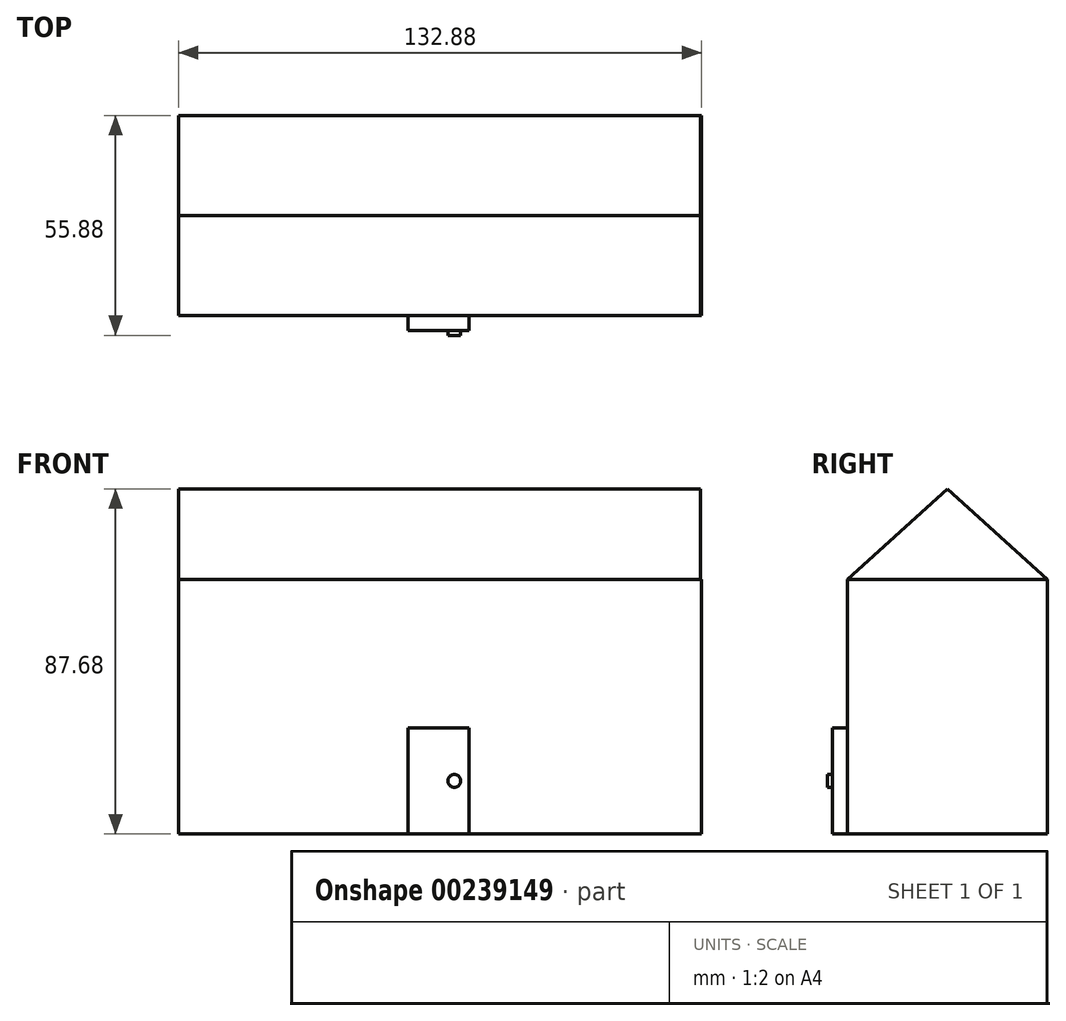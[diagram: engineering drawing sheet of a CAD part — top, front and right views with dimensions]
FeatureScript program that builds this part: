
annotation { "Feature Type Name" : "Feature", "Feature Type Description" : "" }
export const myFeature = defineFeature(function(context is Context, id is Id, definition is map)
    precondition{}
    {
        {
            var Q0;
            Q0=qCreatedBy(makeId("Front.planeOp"),FACE);
            var sketch = newSketch(context, id + "F0", { "sketchPlane" : qUnion([Q0])});
            skLineSegment(sketch, "E0.bottom", {"start": v(-66.44, 32.31) * mm, "end": v(66.44, 32.31) * mm});
            skLineSegment(sketch, "E0.top", {"start": v(-66.44, -32.31) * mm, "end": v(66.44, -32.31) * mm});
            skLineSegment(sketch, "E0.left", {"start": v(-66.44, 32.31) * mm, "end": v(-66.44, -32.31) * mm});
            skLineSegment(sketch, "E0.right", {"start": v(66.44, 32.31) * mm, "end": v(66.44, -32.31) * mm});
            skPoint(sketch, "E0.middle", {"position": v(0, 0) * mm});
            skSolve(sketch);
        }
        {
            var Q0;
            Q0 = qSketchRegion(id + "F0", true);
            extrude(context, id + "F1", {"entities" : qUnion([Q0]), "endBound" : BoundingType.SYMMETRIC, "depth" : 50.8 * mm});
        }
        {
            var Q0;
            Q0=makeQuery(id+"F1.opExtrude","CAP_FACE",FACE,{"disambiguationData":[OSD([sQuery(id+"F0.wireOp",EDGE,"E0.bottom"),sQuery(id+"F0.wireOp",EDGE,"E0.top"),sQuery(id+"F0.wireOp",EDGE,"E0.left"),sQuery(id+"F0.wireOp",EDGE,"E0.right")])],"isStart":false});
            var sketch = newSketch(context, id + "F2", { "sketchPlane" : qUnion([Q0])});
            skLineSegment(sketch, "E1.bottom", {"start": v(7.28, -32.31) * mm, "end": v(-8.2, -32.31) * mm});
            skLineSegment(sketch, "E1.top", {"start": v(7.28, -5.3) * mm, "end": v(-8.2, -5.3) * mm});
            skLineSegment(sketch, "E1.left", {"start": v(7.28, -32.31) * mm, "end": v(7.28, -5.3) * mm});
            skLineSegment(sketch, "E1.right", {"start": v(-8.2, -32.31) * mm, "end": v(-8.2, -5.3) * mm});
            skSolve(sketch);
        }
        {
            var Q0;
            Q0 = qSketchRegion(id + "F2", true);
            extrude(context, id + "F3", {"entities" : qUnion([Q0]), "operationType" : NewBodyOperationType.ADD, "depth" : 3.8 * mm});
        }
        {
            var Q0;
            Q0=makeQuery(id+"F3.opExtrude","CAP_FACE",FACE,{"disambiguationData":[OSD([sQuery(id+"F2.wireOp",EDGE,"E1.bottom"),sQuery(id+"F2.wireOp",EDGE,"E1.top"),sQuery(id+"F2.wireOp",EDGE,"E1.left"),sQuery(id+"F2.wireOp",EDGE,"E1.right")])],"isStart":false});
            var sketch = newSketch(context, id + "F4", { "sketchPlane" : qUnion([Q0])});
            skCircle(sketch, "E2", {"center": v(3.6, -18.81) * mm, "radius": 1.63 * mm});
            skPoint(sketch, "E2.centerSnap0", {"position": v(7.28, -18.81) * mm});
            skSolve(sketch);
        }
        {
            var Q0;
            Q0 = qSketchRegion(id + "F4", true);
            extrude(context, id + "F5", {"entities" : qUnion([Q0]), "operationType" : NewBodyOperationType.ADD, "depth" : 1.27 * mm});
        }
        {
            var Q0;
            Q0=makeQuery(id+"F1.opExtrude","SWEPT_FACE",FACE,{"disambiguationData":[OSD([sQuery(id+"F0.wireOp",EDGE,"E0.left")])]});
            var sketch = newSketch(context, id + "F6", { "sketchPlane" : qUnion([Q0])});
            skLineSegment(sketch, "E3", {"start": v(0, 32.31) * mm, "end": v(0, 55.37) * mm, "construction": true});
            skPoint(sketch, "E3.endSnap0", {"position": v(0, 32.31) * mm});
            skLineSegment(sketch, "E4", {"start": v(0, 55.37) * mm, "end": v(25.4, 32.31) * mm});
            skLineSegment(sketch, "E5", {"start": v(25.4, 32.31) * mm, "end": v(-25.4, 32.31) * mm});
            skLineSegment(sketch, "E6", {"start": v(-25.4, 32.31) * mm, "end": v(0, 55.37) * mm});
            skSolve(sketch);
        }
        {
            var Q0;
            Q0 = qSketchRegion(id + "F6", true);
            extrude(context, id + "F7", {"entities" : qUnion([Q0]), "operationType" : NewBodyOperationType.ADD, "oppositeDirection" : true, "depth" : 132.6 * mm});
        }
    });
